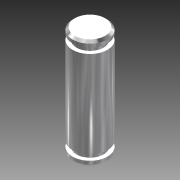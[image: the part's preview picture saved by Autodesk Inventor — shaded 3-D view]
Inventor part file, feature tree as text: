
AUTODESK INVENTOR PART (.ipt)
format: ipt  version: 2014 SP1 (Build 180222100, 222)  size: 151,040 bytes
history: native  units: in
note: dims shown in document units (in); Inventor stores cm internally (conversion verified against a paired STEP export)
features: other x1, imported_body x1, extrude x1, sketch x1, projected_geometry x1
ambient origin geometry x8: Origin, YZ Plane, XZ Plane, XY Plane, X Axis, Y Axis, Z Axis, Center Point
bodies: Body1 (feature_tree)
feature tree (5):
  parser-record x1  (decoder bookkeeping rows leaked as tree rows — omitted from the tree; the rows remain in map.json)
  imported_body  "Base1"
  extrude  "Extrusion1"  [1 undecoded]
  sketch  "Sketch1"  dims[d4=0.3937in d5=0.0in]
  projected_geometry  "Projected Loop1"
note: 1 required parameter value undecoded (feature->parameter linkage not recoverable at this tier; creation-order binding heuristic only, values carry confidence <= 0.55)
